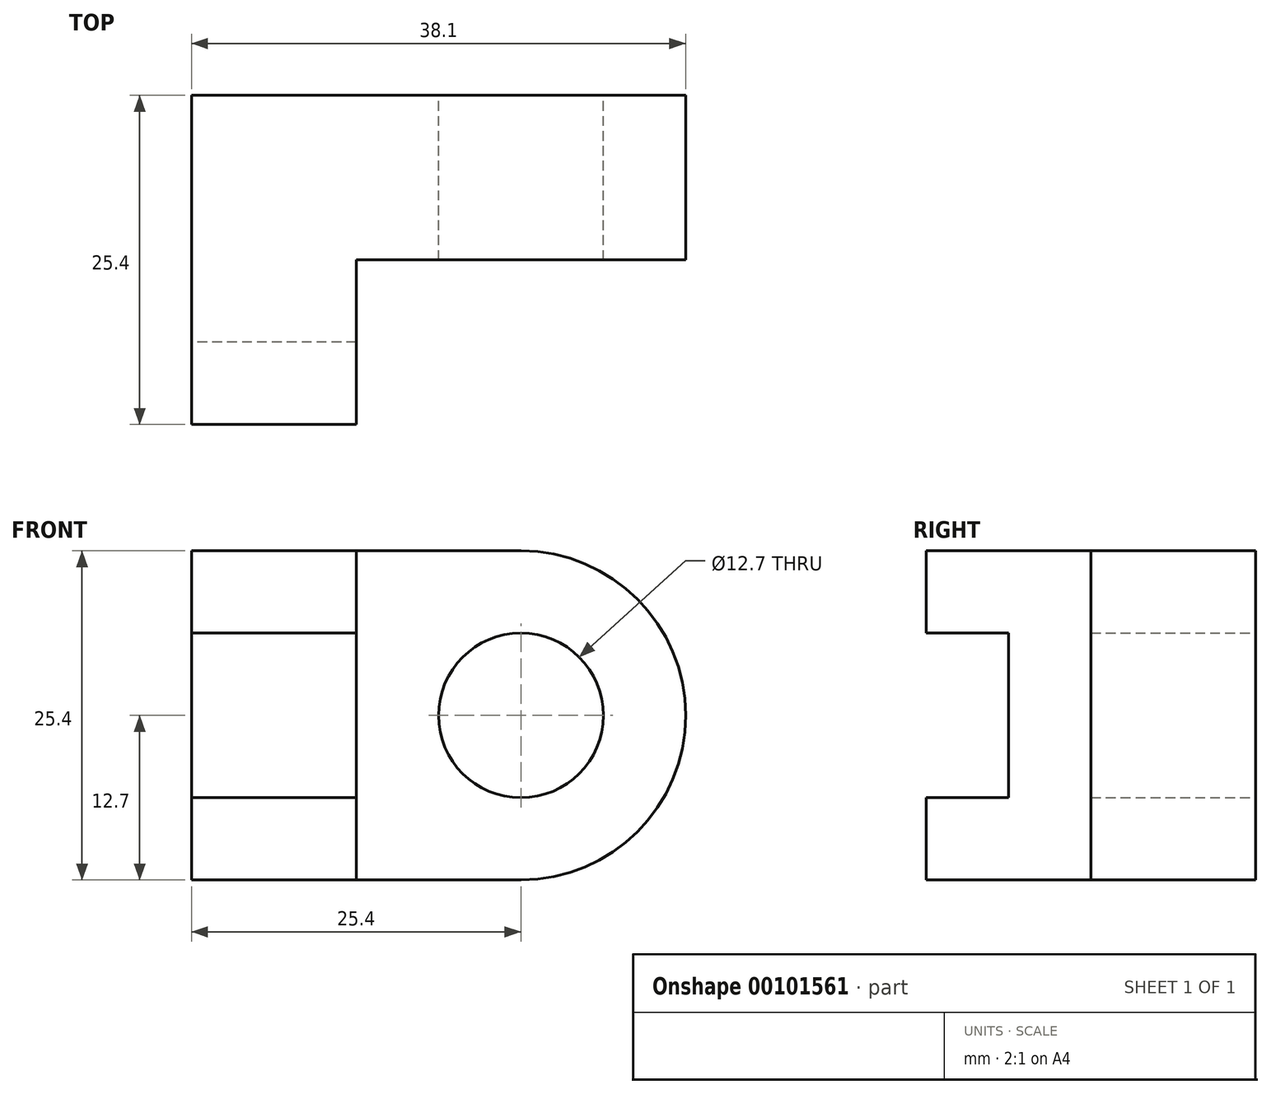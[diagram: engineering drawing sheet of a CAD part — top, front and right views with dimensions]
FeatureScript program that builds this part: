
annotation { "Feature Type Name" : "Feature", "Feature Type Description" : "" }
export const myFeature = defineFeature(function(context is Context, id is Id, definition is map)
    precondition{}
    {
        {
            var Q0;
            Q0=qCreatedBy(makeId("Front.planeOp"),FACE);
            var sketch = newSketch(context, id + "F0", { "sketchPlane" : qUnion([Q0])});
            skLineSegment(sketch, "E0", {"start": v(0, 0) * mm, "end": v(25.4, 0) * mm});
            skLineSegment(sketch, "E1", {"start": v(0, 0) * mm, "end": v(0, -25.4) * mm});
            skLineSegment(sketch, "E2", {"start": v(0, -25.4) * mm, "end": v(25.4, -25.4) * mm});
            skArc(sketch, "E3", {"start": v(25.4, -25.4) * mm, "mid": v(38.1, -12.7) * mm, "end": v(25.4, 0) * mm});
            skCircle(sketch, "E4", {"center": v(25.4, -12.7) * mm, "radius": 6.35 * mm});
            skSolve(sketch);
        }
        {
            var Q0;
            Q0=makeQuery(id+"F0.imprint","IMPRINT",FACE,{"disambiguationData":[TD([[makeQuery(id+"F0.imprint","IMPRINT",EDGE,{"derivedFrom":sQuery(id+"F0.wireOp",EDGE,"E0")}),-1.0]])]});
            extrude(context, id + "F1", {"entities" : qUnion([Q0]), "depth" : 12.7 * mm});
        }
        {
            var Q0;
            Q0=qCreatedBy(makeId("Right.planeOp"),FACE);
            var sketch = newSketch(context, id + "F2", { "sketchPlane" : qUnion([Q0])});
            skLineSegment(sketch, "E5", {"start": v(0, 0) * mm, "end": v(-25.4, 0) * mm});
            skLineSegment(sketch, "E6", {"start": v(-25.4, 0) * mm, "end": v(-25.4, -6.35) * mm});
            skLineSegment(sketch, "E7", {"start": v(-25.4, -6.35) * mm, "end": v(-19.05, -6.35) * mm});
            skLineSegment(sketch, "E8", {"start": v(-19.05, -6.35) * mm, "end": v(-19.05, -19.05) * mm});
            skLineSegment(sketch, "E9", {"start": v(-19.05, -19.05) * mm, "end": v(-25.4, -19.05) * mm});
            skLineSegment(sketch, "E10", {"start": v(-25.4, -19.05) * mm, "end": v(-25.4, -25.4) * mm});
            skLineSegment(sketch, "E11", {"start": v(-25.4, -25.4) * mm, "end": v(0, -25.4) * mm});
            skLineSegment(sketch, "E12", {"start": v(0, -25.4) * mm, "end": v(0, 0) * mm});
            skSolve(sketch);
        }
        {
            var Q0;
            Q0=makeQuery(id+"F2.imprint","IMPRINT",FACE,{"disambiguationData":[TD([[makeQuery(id+"F2.imprint","IMPRINT",EDGE,{"derivedFrom":sQuery(id+"F2.wireOp",EDGE,"E5")}),1.0]])]});
            extrude(context, id + "F3", {"entities" : qUnion([Q0]), "operationType" : NewBodyOperationType.ADD, "depth" : 12.7 * mm});
        }
    });
